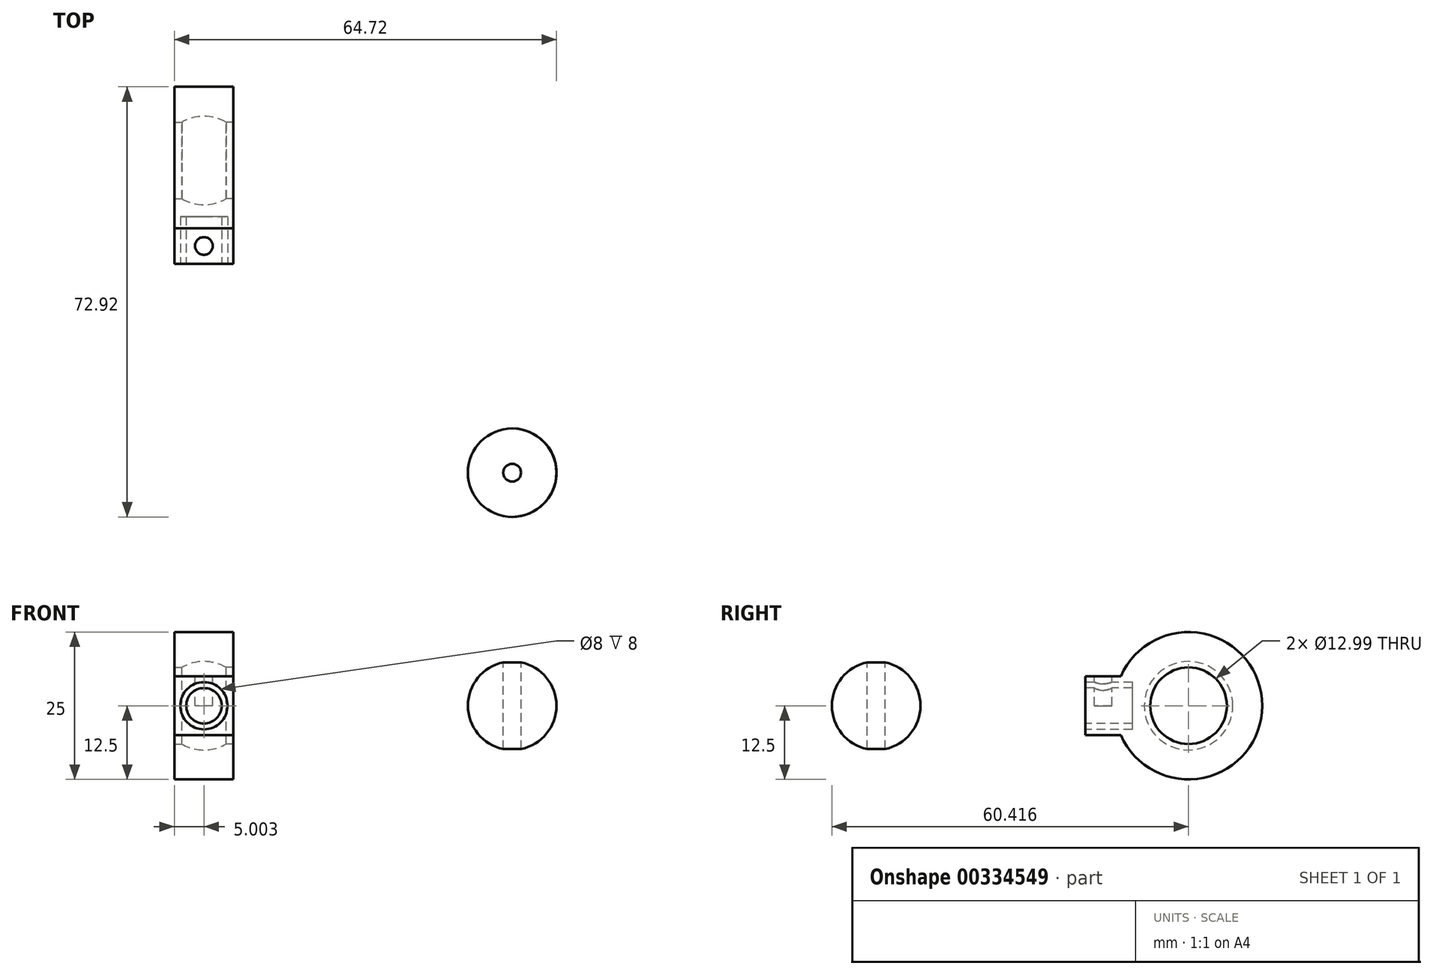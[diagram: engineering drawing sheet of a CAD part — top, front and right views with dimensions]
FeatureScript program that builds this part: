
annotation { "Feature Type Name" : "Feature", "Feature Type Description" : "" }
export const myFeature = defineFeature(function(context is Context, id is Id, definition is map)
    precondition{}
    {
        {
            var Q0;
            Q0=qCreatedBy(makeId("Top.planeOp"),FACE);
            var sketch = newSketch(context, id + "F0", { "sketchPlane" : qUnion([Q0])});
            skCircle(sketch, "E0", {"center": v(0, 0) * mm, "radius": 7.5 * mm});
            skLineSegment(sketch, "E1", {"start": v(0, 0) * mm, "end": v(0, 7.5) * mm});
            skLineSegment(sketch, "E2", {"start": v(0, 7.5) * mm, "end": v(0, -7.5) * mm});
            skSolve(sketch);
        }
        {
            var Q0;
            {var subQ0=sQuery(id+"F0.wireOp",EDGE,"E2");var subQ4=makeQuery(id+"F0.imprint","IMPRINT",VERTEX,{"derivedFrom":subQ0});Q0=makeQuery(id+"F0.imprint","IMPRINT",FACE,{"disambiguationData":[TD([[makeQuery(id+"F0.imprint","IMPRINT",EDGE,{"disambiguationData":[TD([[subQ4,1.0]])],"derivedFrom":subQ0}),1.0]])]});}
            var Q1;
            Q1=sQuery(id+"F0.wireOp",EDGE,"E2");
            revolve(context, id + "F1", {"entities" : qUnion([Q0]), "axis" : qUnion([Q1]), "revolveType" : RevolveType.FULL});
        }
        {
            var Q0;
            Q0=qCreatedBy(makeId("Top.planeOp"),FACE);
            var sketch = newSketch(context, id + "F2", { "sketchPlane" : qUnion([Q0])});
            skCircle(sketch, "E3", {"center": v(0, 0) * mm, "radius": 1.5 * mm});
            skSolve(sketch);
        }
        {
            var Q0;
            Q0 = qSketchRegion(id + "F2", true);
            extrude(context, id + "F3", {"entities" : qUnion([Q0]), "operationType" : NewBodyOperationType.REMOVE, "oppositeDirection" : true, "depth" : 17.5 * mm, "hasSecondDirection" : true, "secondDirectionOppositeDirection" : false, "secondDirectionDepth" : 25 * mm});
        }
        {
            var Q0;
            Q0=qCreatedBy(makeId("Top.planeOp"),FACE);
            var sketch = newSketch(context, id + "F4", { "sketchPlane" : qUnion([Q0])});
            skArc(sketch, "E4", {"start": v(-48.47, 59.41) * mm, "mid": v(-52.22, 60.42) * mm, "end": v(-55.97, 59.41) * mm});
            skLineSegment(sketch, "E5.left", {"start": v(-48.47, 52.92) * mm, "end": v(-48.47, 59.41) * mm});
            skLineSegment(sketch, "E5.right", {"start": v(-55.97, 52.92) * mm, "end": v(-55.97, 59.41) * mm});
            skLineSegment(sketch, "E6", {"start": v(-55.97, 59.41) * mm, "end": v(-55.97, 60.82) * mm});
            skLineSegment(sketch, "E7", {"start": v(-48.47, 59.41) * mm, "end": v(-48.47, 60.82) * mm});
            skArc(sketch, "E8.trimOffspring", {"start": v(-48.47, 60.82) * mm, "mid": v(-52.22, 61.67) * mm, "end": v(-55.97, 60.82) * mm});
            skLineSegment(sketch, "E9", {"start": v(-55.97, 60.82) * mm, "end": v(-55.97, 64.84) * mm});
            skLineSegment(sketch, "E10", {"start": v(-48.47, 60.82) * mm, "end": v(-48.47, 64.84) * mm});
            skLineSegment(sketch, "E11.top", {"start": v(-48.47, 65.42) * mm, "end": v(-55.97, 65.42) * mm});
            skLineSegment(sketch, "E11.left", {"start": v(-48.47, 64.84) * mm, "end": v(-48.47, 65.42) * mm});
            skLineSegment(sketch, "E11.right", {"start": v(-55.97, 64.84) * mm, "end": v(-55.97, 65.42) * mm});
            skLineSegment(sketch, "E12", {"start": v(-52.22, 52.92) * mm, "end": v(-48.47, 52.92) * mm});
            skLineSegment(sketch, "E13", {"start": v(-48.47, 52.92) * mm, "end": v(-55.97, 52.92) * mm});
            skSolve(sketch);
        }
        {
            var Q0;
            Q0=makeQuery(id+"F4.imprint","IMPRINT",FACE,{"disambiguationData":[TD([[makeQuery(id+"F4.imprint","IMPRINT",EDGE,{"derivedFrom":sQuery(id+"F4.wireOp",EDGE,"E8.trimOffspring")}),-1.0]])]});
            var Q1;
            Q1=makeQuery(id+"F4.imprint","IMPRINT",FACE,{"disambiguationData":[TD([[makeQuery(id+"F4.imprint","IMPRINT",EDGE,{"derivedFrom":sQuery(id+"F4.wireOp",EDGE,"E4")}),-1.0]])]});
            var Q2;
            Q2=sQuery(id+"F4.wireOp",EDGE,"E13");
            revolve(context, id + "F5", {"entities" : qUnion([Q0, Q1]), "axis" : qUnion([Q2]), "revolveType" : RevolveType.FULL});
        }
        {
            var Q0;
            Q0=makeQuery(id+"F5.opRevolve","SWEPT_FACE",FACE,{"disambiguationData":[OSD([sQuery(id+"F4.wireOp",EDGE,"E6"),sQuery(id+"F4.wireOp",EDGE,"E9"),sQuery(id+"F4.wireOp",EDGE,"E11.right")])]});
            var sketch = newSketch(context, id + "F6", { "sketchPlane" : qUnion([Q0])});
            skLineSegment(sketch, "E14", {"start": v(-52.92, 0) * mm, "end": v(-40.42, 0) * mm});
            skLineSegment(sketch, "E15.bottom", {"start": v(-35.42, -5) * mm, "end": v(-45.42, -5) * mm});
            skLineSegment(sketch, "E15.top", {"start": v(-35.42, 5) * mm, "end": v(-45.42, 5) * mm});
            skLineSegment(sketch, "E15.left", {"start": v(-35.42, -5) * mm, "end": v(-35.42, 5) * mm});
            skLineSegment(sketch, "E15.right", {"start": v(-45.42, -5) * mm, "end": v(-45.42, 5) * mm});
            skPoint(sketch, "E15.middle", {"position": v(-40.42, 0) * mm});
            skSolve(sketch);
        }
        {
            var Q0;
            {var subQ4=sQuery(id+"F6.wireOp",EDGE,"E15.left");Q0=makeQuery(id+"F6.imprint","IMPRINT",FACE,{"disambiguationData":[TD([[makeQuery(id+"F6.imprint","IMPRINT",EDGE,{"derivedFrom":subQ4}),1.0]])]});}
            var Q1;
            Q1=makeQuery(id+"F5.opRevolve","SWEPT_FACE",FACE,{"disambiguationData":[OSD([sQuery(id+"F4.wireOp",EDGE,"E7"),sQuery(id+"F4.wireOp",EDGE,"E10"),sQuery(id+"F4.wireOp",EDGE,"E11.left")])]});
            extrude(context, id + "F7", {"entities" : qUnion([Q0]), "operationType" : NewBodyOperationType.ADD, "endBound" : BoundingType.UP_TO_SURFACE, "oppositeDirection" : true, "endBoundEntityFace" : qUnion([Q1]), "depth" : 25 * mm});
        }
        {
            var Q0;
            {var subQ0=sQuery(id+"F4.wireOp",EDGE,"E11.left");var subQ1=sQuery(id+"F4.wireOp",EDGE,"E10");var subQ2=sQuery(id+"F4.wireOp",EDGE,"E7");Q0=makeQuery(id+"F7.boolean.opBoolean","MERGE",FACE,{"derivedFrom":[makeQuery(id+"F5.opRevolve","SWEPT_FACE",FACE,{"disambiguationData":[OSD([subQ2,subQ1,subQ0])]}),makeQuery(id+"F7.opExtrude","CAP_FACE",FACE,{"disambiguationData":[OSD([subQ2,subQ1,subQ0])],"isStart":false})]});}
            extrude(context, id + "F8", {"entities" : qUnion([Q0]), "operationType" : NewBodyOperationType.ADD, "depth" : 1.25 * mm});
        }
        {
            var Q0;
            {var subQ0=sQuery(id+"F4.wireOp",EDGE,"E11.right");Q0=makeQuery(id+"F7.boolean.opBoolean","MERGE",FACE,{"derivedFrom":[makeQuery(id+"F5.opRevolve","SWEPT_FACE",FACE,{"disambiguationData":[OSD([sQuery(id+"F4.wireOp",EDGE,"E6"),sQuery(id+"F4.wireOp",EDGE,"E9"),subQ0])]}),makeQuery(id+"F7.opExtrude","CAP_FACE",FACE,{"disambiguationData":[OSD([sQuery(id+"F4.wireOp",EDGE,"E11.top"),subQ0,sQuery(id+"F6.wireOp",EDGE,"E15.bottom"),sQuery(id+"F6.wireOp",EDGE,"E15.top"),sQuery(id+"F6.wireOp",EDGE,"E15.left")])],"isStart":true})]});}
            extrude(context, id + "F9", {"entities" : qUnion([Q0]), "operationType" : NewBodyOperationType.ADD, "depth" : 1.25 * mm});
        }
        {
            var Q0;
            {var subQ0=sQuery(id+"F6.wireOp",EDGE,"E15.left");Q0=makeQuery(id+"F9.boolean.opBoolean","MERGE",FACE,{"derivedFrom":[makeQuery(id+"F8.boolean.opBoolean","MERGE",FACE,{"derivedFrom":[makeQuery(id+"F7.opExtrude","SWEPT_FACE",FACE,{"disambiguationData":[OSD([subQ0])]}),makeQuery(id+"F8.opExtrude","SWEPT_FACE",FACE,{"disambiguationData":[OSD([sQuery(id+"F4.wireOp",EDGE,"E7"),sQuery(id+"F4.wireOp",EDGE,"E10"),sQuery(id+"F4.wireOp",EDGE,"E11.left"),subQ0])]})]}),makeQuery(id+"F9.opExtrude","SWEPT_FACE",FACE,{"disambiguationData":[OSD([subQ0])]})]});}
            var sketch = newSketch(context, id + "F10", { "sketchPlane" : qUnion([Q0])});
            skCircle(sketch, "E16", {"center": v(-52.22, 0) * mm, "radius": 4 * mm});
            skPoint(sketch, "E16.centerSnap0", {"position": v(-57.22, 0) * mm});
            skPoint(sketch, "E16.centerSnap1", {"position": v(-52.22, 5) * mm});
            skCircle(sketch, "E17", {"center": v(-52.22, 0) * mm, "radius": 3 * mm});
            skSolve(sketch);
        }
        {
            var Q0;
            Q0=makeQuery(id+"F10.imprint","IMPRINT",FACE,{"disambiguationData":[TD([[makeQuery(id+"F10.imprint","IMPRINT",EDGE,{"derivedFrom":sQuery(id+"F10.wireOp",EDGE,"E16")}),1.0]])]});
            extrude(context, id + "F11", {"entities" : qUnion([Q0]), "operationType" : NewBodyOperationType.REMOVE, "oppositeDirection" : true, "depth" : 8 * mm});
        }
        {
            var Q0;
            {var subQ0=sQuery(id+"F6.wireOp",EDGE,"E15.top");Q0=makeQuery(id+"F9.boolean.opBoolean","MERGE",FACE,{"derivedFrom":[makeQuery(id+"F8.boolean.opBoolean","MERGE",FACE,{"derivedFrom":[makeQuery(id+"F7.opExtrude","SWEPT_FACE",FACE,{"disambiguationData":[OSD([subQ0])]}),makeQuery(id+"F8.opExtrude","SWEPT_FACE",FACE,{"disambiguationData":[OSD([sQuery(id+"F4.wireOp",EDGE,"E7"),sQuery(id+"F4.wireOp",EDGE,"E10"),sQuery(id+"F4.wireOp",EDGE,"E11.left"),subQ0])]})]}),makeQuery(id+"F9.opExtrude","SWEPT_FACE",FACE,{"disambiguationData":[OSD([subQ0])]})]});}
            var sketch = newSketch(context, id + "F12", { "sketchPlane" : qUnion([Q0])});
            skCircle(sketch, "E18", {"center": v(-52.22, 38.44) * mm, "radius": 1.5 * mm});
            skPoint(sketch, "E18.centerSnap0", {"position": v(-52.22, 35.42) * mm});
            skPoint(sketch, "E18.centerSnap1", {"position": v(-57.22, 38.44) * mm});
            skSolve(sketch);
        }
        {
            var Q0;
            Q0 = qSketchRegion(id + "F12", true);
            extrude(context, id + "F13", {"entities" : qUnion([Q0]), "operationType" : NewBodyOperationType.REMOVE, "oppositeDirection" : true, "depth" : 5 * mm});
        }
    });
